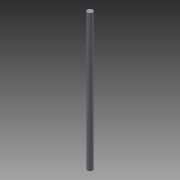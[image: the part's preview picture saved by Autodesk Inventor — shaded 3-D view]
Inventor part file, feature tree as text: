
AUTODESK INVENTOR PART (.ipt)
format: ipt  version: 2015 SP1 (Build 190203100, 203)  size: 64,000 bytes
history: native  units: mm
features: extrude x1, sketch x1
ambient origin geometry x8: Origin, YZ Plane, XZ Plane, XY Plane, X Axis, Y Axis, Z Axis, Center Point
bodies: Solid1 (feature_tree)
feature tree (2):
  extrude  "Extrusion1"  Depth=103.6mm TaperAngle=0.0deg
  sketch  "Sketch1"  dims[d0=4.0mm d1=103.6mm d2=0.0mm]
